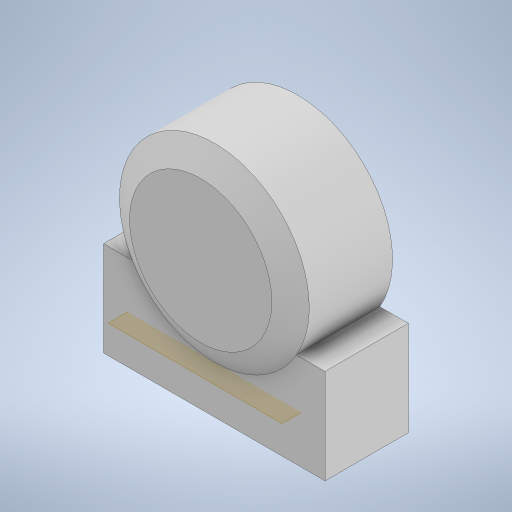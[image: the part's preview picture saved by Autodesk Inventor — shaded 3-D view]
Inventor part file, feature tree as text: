
AUTODESK INVENTOR PART (.ipt)
format: ipt  version: 2023 (Build 270158000, 158)  size: 243,712 bytes
history: native  units: in
note: dims shown in document units (in); Inventor stores cm internally (conversion verified against a paired STEP export)
features: extrude x2, chamfer x2, sketch x2, plane x1
ambient origin geometry x8: Origin, YZ Plane, XZ Plane, XY Plane, X Axis, Y Axis, Z Axis, Center Point
bodies: Body1 (feature_tree)
feature tree (7):
  extrude  "Extrusion2"  Depth=3.5in TaperAngle=0.0deg
  chamfer  "Chamfer1"  Distance=0.75in Angle=30.0deg
  chamfer  "Chamfer2"  Distance=0.75in Angle=30.0deg
  plane  "Work Plane1"
  extrude  "Extrusion11"  Depth=3.5in
  sketch  "Sketch2"  dims[d7=6.0in d8=3.5in d9=0.0in d10=0.75in d11=0.125in d12=30.0deg d13=0.75in d14=0.125in d15=30.0deg]
  sketch  "Sketch10"  dims[d44=3.0in d45=0.0in d46=3.5in d47=3.5in d6=0.5in d41=0.5in d42=0.0344in d43=0.5in d48=0.5in d49=0.0344in]
